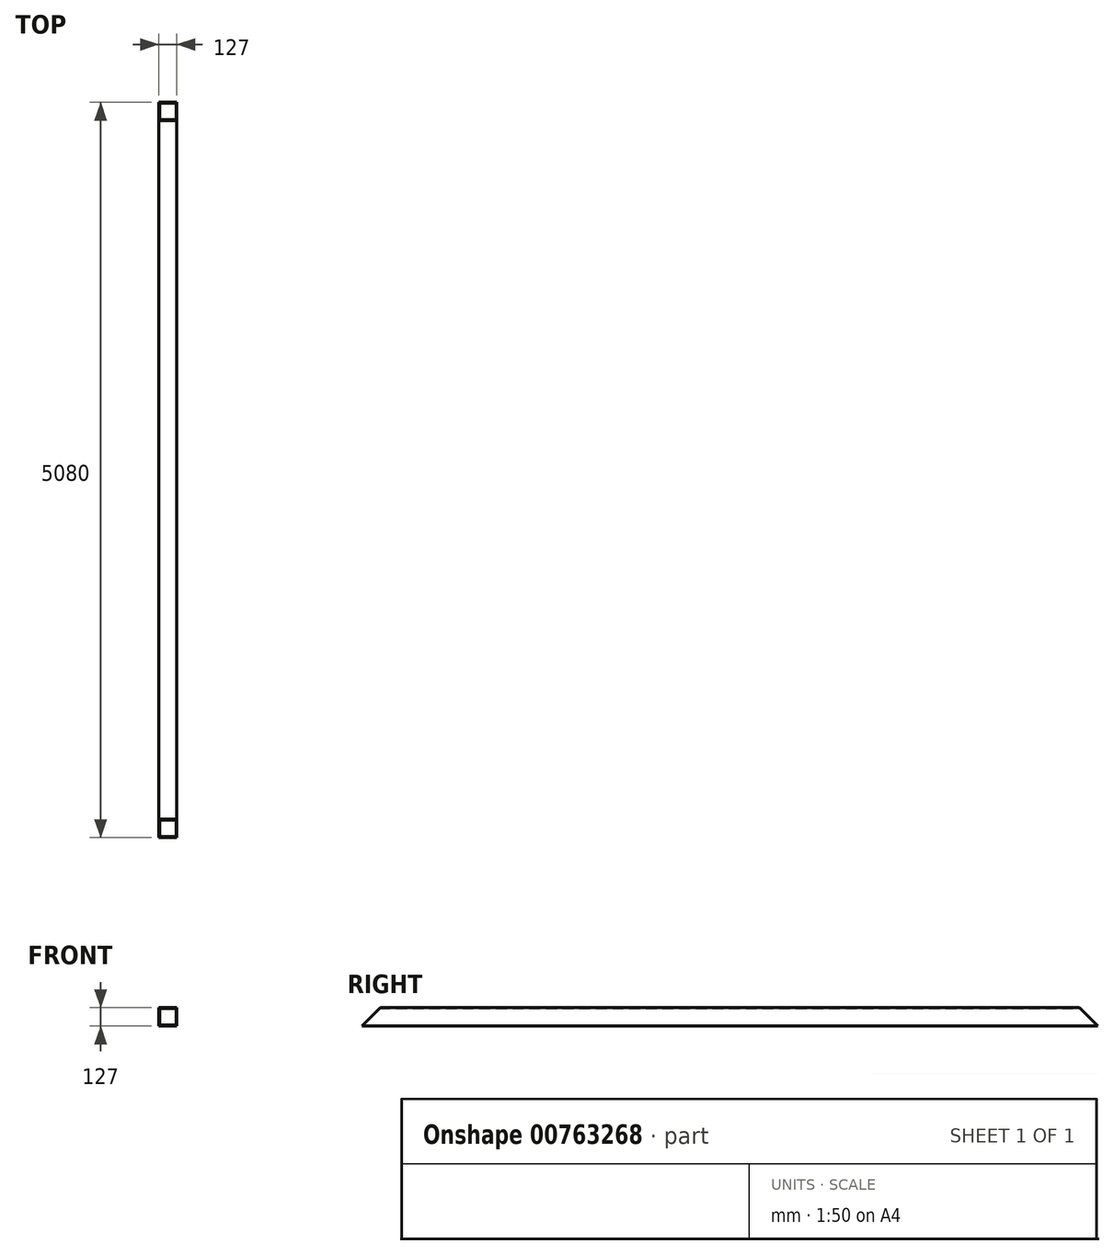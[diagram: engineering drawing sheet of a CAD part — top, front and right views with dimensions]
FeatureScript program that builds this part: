
annotation { "Feature Type Name" : "Feature", "Feature Type Description" : "" }
export const myFeature = defineFeature(function(context is Context, id is Id, definition is map)
    precondition{}
    {
        {
            var Q0;
            Q0=qCreatedBy(makeId("Front.planeOp"),FACE);
            var sketch = newSketch(context, id + "F0", { "sketchPlane" : qUnion([Q0])});
            skLineSegment(sketch, "E0.bottom", {"start": v(-63.5, 63.5) * mm, "end": v(63.5, 63.5) * mm});
            skLineSegment(sketch, "E0.top", {"start": v(-63.5, -63.5) * mm, "end": v(63.5, -63.5) * mm});
            skLineSegment(sketch, "E0.left", {"start": v(-63.5, 63.5) * mm, "end": v(-63.5, -63.5) * mm});
            skLineSegment(sketch, "E0.right", {"start": v(63.5, 63.5) * mm, "end": v(63.5, -63.5) * mm});
            skLineSegment(sketch, "E1.bottom", {"start": v(-57.15, 57.15) * mm, "end": v(57.15, 57.15) * mm});
            skLineSegment(sketch, "E1.top", {"start": v(-57.15, -57.15) * mm, "end": v(57.15, -57.15) * mm});
            skLineSegment(sketch, "E1.left", {"start": v(-57.15, 57.15) * mm, "end": v(-57.15, -57.15) * mm});
            skLineSegment(sketch, "E1.right", {"start": v(57.15, 57.15) * mm, "end": v(57.15, -57.15) * mm});
            skLineSegment(sketch, "E2", {"start": v(-57.15, 57.15) * mm, "end": v(57.15, -57.15) * mm, "construction": true});
            skLineSegment(sketch, "E3", {"start": v(63.5, 63.5) * mm, "end": v(-63.5, -63.5) * mm, "construction": true});
            skSolve(sketch);
        }
        {
            var Q0;
            Q0 = qSketchRegion(id + "F0", true);
            extrude(context, id + "F1", {"entities" : qUnion([Q0]), "endBound" : BoundingType.SYMMETRIC, "depth" : 5080 * mm, "offsetDistance" : 25.4 * mm});
        }
        {
            var Q0;
            Q0=makeQuery(id+"F1.opExtrude","SWEPT_FACE",FACE,{"disambiguationData":[OSD([sQuery(id+"F0.wireOp",EDGE,"E0.right")])]});
            var sketch = newSketch(context, id + "F2", { "sketchPlane" : qUnion([Q0])});
            skLineSegment(sketch, "E4", {"start": v(-2540, -63.5) * mm, "end": v(-2540, 63.5) * mm});
            skLineSegment(sketch, "E5", {"start": v(-2540, 63.5) * mm, "end": v(-2413, 63.5) * mm});
            skLineSegment(sketch, "E6", {"start": v(-2413, 63.5) * mm, "end": v(-2540, -63.5) * mm});
            skLineSegment(sketch, "E7", {"start": v(2540, -63.5) * mm, "end": v(2413, 63.5) * mm});
            skLineSegment(sketch, "E8", {"start": v(2413, 63.5) * mm, "end": v(2540, 63.5) * mm});
            skLineSegment(sketch, "E9", {"start": v(2540, 63.5) * mm, "end": v(2540, -63.5) * mm});
            skSolve(sketch);
        }
        {
            var Q0;
            Q0 = qSketchRegion(id + "F2", true);
            extrude(context, id + "F3", {"entities" : qUnion([Q0]), "operationType" : NewBodyOperationType.REMOVE, "endBound" : BoundingType.THROUGH_ALL, "oppositeDirection" : true, "depth" : 25.4 * mm, "offsetDistance" : 25.4 * mm});
        }
    });
